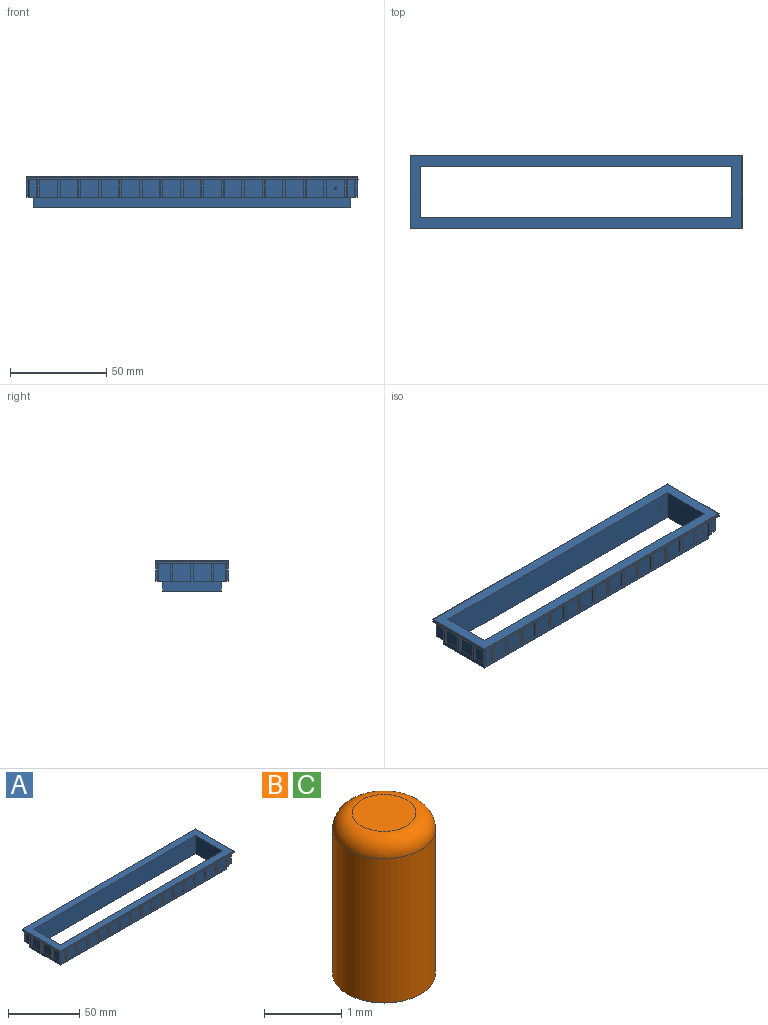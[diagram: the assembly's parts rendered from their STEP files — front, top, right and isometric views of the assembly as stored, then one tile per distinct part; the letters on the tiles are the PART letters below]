
ASSEMBLY  parts=3 mates=2
PART A: 299 faces, bbox 172.7x38.1x15.7 mm
  f0: plane 9.38x1.14mm, normal (0,0,-1), area 10.4mm2, adj f62,f134,f136,f254,f255,f288
  f1: plane 9.38x1.14mm, normal (0,0,-1), area 10.4mm2, adj f63,f131,f133,f256,f257,f288
  f2: plane 9.38x1.14mm, normal (0,0,-1), area 10.4mm2, adj f64,f128,f130,f258,f259,f288
  f3: plane 9.38x1.14mm, normal (0,0,-1), area 10.4mm2, adj f65,f125,f127,f260,f261,f288
  f4: plane 9.38x1.14mm, normal (0,0,-1), area 10.4mm2, adj f66,f122,f124,f262,f263,f288
  f5: plane 9.38x1.14mm, normal (0,0,-1), area 10.4mm2, adj f67,f119,f121,f264,f265,f288
  f6: plane 9.38x1.14mm, normal (0,0,-1), area 10.4mm2, adj f68,f116,f118,f266,f267,f288
  f7: plane 9.38x1.14mm, normal (0,0,-1), area 10.4mm2, adj f69,f113,f115,f268,f269,f288
  f8: plane 9.38x1.14mm, normal (0,0,-1), area 10.4mm2, adj f70,f110,f112,f270,f271,f288
  f9: plane 9.38x1.14mm, normal (0,0,-1), area 10.4mm2, adj f71,f107,f109,f272,f273,f288
  f10: plane 9.38x1.14mm, normal (0,0,-1), area 10.4mm2, adj f72,f104,f106,f274,f275,f288
  f11: plane 9.38x1.14mm, normal (0,0,-1), area 10.4mm2, adj f73,f101,f103,f276,f277,f288
  f12: plane 9.38x1.14mm, normal (0,0,-1), area 10.4mm2, adj f74,f98,f100,f278,f279,f288
  f13: plane 9.38x1.14mm, normal (0,0,-1), area 10.4mm2, adj f75,f95,f97,f280,f281,f288
  f14: plane 9.38x1.14mm, normal (0,0,-1), area 10.4mm2, adj f76,f91,f94,f282,f283,f288
  f15: plane 7.64x5.72mm, normal (0,0,-1), area 13.7mm2, adj f77,f81,f93,f195,f216,f284,f286,f288
  f16: plane 9.38x1.14mm, normal (0,0,-1), area 10.4mm2, adj f43,f192,f194,f215,f218,f286
  f17: plane 9.38x1.14mm, normal (0,0,-1), area 10.4mm2, adj f44,f189,f191,f217,f220,f286
  f18: plane 7.64x5.72mm, normal (0,0,-1), area 13.7mm2, adj f45,f51,f169,f188,f219,f231,f285,f286
  f19: plane 9.38x1.14mm, normal (0,0,-1), area 10.4mm2, adj f59,f145,f170,f232,f247,f285
  f20: plane 9.38x1.14mm, normal (0,0,-1), area 10.4mm2, adj f52,f147,f166,f233,f248,f285
  f21: plane 9.38x1.14mm, normal (0,0,-1), area 10.4mm2, adj f49,f168,f175,f227,f234,f285
  f22: plane 9.38x1.14mm, normal (0,0,-1), area 10.4mm2, adj f61,f139,f176,f228,f251,f285
  f23: plane 9.38x1.14mm, normal (0,0,-1), area 10.4mm2, adj f57,f140,f151,f243,f252,f285
  f24: plane 9.38x1.14mm, normal (0,0,-1), area 10.4mm2, adj f46,f153,f184,f221,f244,f285
  f25: plane 9.38x1.14mm, normal (0,0,-1), area 10.4mm2, adj f60,f142,f186,f222,f249,f285
  f26: plane 9.38x1.14mm, normal (0,0,-1), area 10.4mm2, adj f54,f144,f160,f237,f250,f285
  f27: plane 9.38x1.14mm, normal (0,0,-1), area 10.4mm2, adj f47,f162,f181,f223,f238,f285
  f28: plane 9.38x1.14mm, normal (0,0,-1), area 10.4mm2, adj f58,f148,f182,f224,f245,f285
  f29: plane 9.38x1.14mm, normal (0,0,-1), area 10.4mm2, adj f48,f150,f178,f225,f246,f285
  f30: plane 9.38x1.14mm, normal (0,0,-1), area 10.4mm2, adj f50,f172,f179,f226,f229,f285
  f31: plane 9.38x1.14mm, normal (0,0,-1), area 10.4mm2, adj f55,f157,f173,f230,f239,f285
  f32: plane 9.38x1.14mm, normal (0,0,-1), area 10.4mm2, adj f56,f154,f159,f240,f241,f285
  f33: plane 9.38x1.14mm, normal (0,0,-1), area 10.4mm2, adj f53,f155,f163,f235,f242,f285
  f34: plane 7.64x5.69mm, normal (0,0,-1), area 13.7mm2, adj f41,f80,f164,f201,f212,f236,f285,f287
  f35: plane 9.38x1.14mm, normal (0,0,-1), area 10.4mm2, adj f39,f200,f204,f210,f211,f287
  f36: plane 9.38x1.14mm, normal (0,0,-1), area 10.4mm2, adj f42,f198,f203,f209,f214,f287
  f37: plane 165.1x30.48mm, normal (0,0,-1), area 682.8mm2, adj f83,f84,f85,f86,f205,f206,f207,f208
  f38: plane 172.47x37.85mm, normal (0,0,1), area 2177.7mm2, adj f205,f206,f207,f208,f289,f290,f291,f292
  f39: plane 9.13x9.12mm, normal (1,0,0), area 83.2mm2, adj f35,f82,f200,f204
  f40: plane 7.64x5.69mm, normal (0,0,-1), area 13.7mm2, adj f78,f79,f137,f197,f213,f253,f287,f288
  f41: plane 9.12x5.86mm, normal (1,0,0), area 53.4mm2, adj f34,f82,f201,f294
  f42: plane 9.13x9.12mm, normal (1,0,0), area 83.2mm2, adj f36,f82,f198,f203
  f43: plane 9.13x9.12mm, normal (-1,0,0), area 83.2mm2, adj f16,f82,f192,f194
  f44: plane 9.13x9.12mm, normal (-1,0,0), area 83.2mm2, adj f17,f82,f189,f191
  f45: plane 9.12x5.86mm, normal (-1,0,0), area 53.4mm2, adj f18,f82,f188,f295
  f46: plane 9.13x9.12mm, normal (0,1,0), area 83.2mm2, adj f24,f82,f153,f184
  f47: plane 9.13x9.12mm, normal (0,1,0), area 83.2mm2, adj f27,f82,f162,f181
  f48: plane 9.13x9.12mm, normal (0,1,0), area 83.2mm2, adj f29,f82,f150,f178
  f49: plane 9.13x9.12mm, normal (0,1,0), area 83.2mm2, adj f21,f82,f168,f175
  f50: plane 9.13x9.12mm, normal (0,1,0), area 83.2mm2, adj f30,f82,f172,f179
  f51: plane 9.12x3.94mm, normal (0,1,0), area 35.9mm2, adj f18,f82,f169,f295
  f52: plane 9.13x9.12mm, normal (0,1,0), area 83.2mm2, adj f20,f82,f147,f166
  f53: plane 9.13x9.12mm, normal (0,1,0), area 81.7mm2, adj f33,f82,f155,f163,f297
  f54: plane 9.13x9.12mm, normal (0,1,0), area 83.2mm2, adj f26,f82,f144,f160
  f55: plane 9.13x9.12mm, normal (0,1,0), area 83.2mm2, adj f31,f82,f157,f173
  f56: plane 9.13x9.12mm, normal (0,1,0), area 83.2mm2, adj f32,f82,f154,f159
  f57: plane 9.13x9.12mm, normal (0,1,0), area 83.2mm2, adj f23,f82,f140,f151
  f58: plane 9.13x9.12mm, normal (0,1,0), area 83.2mm2, adj f28,f82,f148,f182
  f59: plane 9.13x9.12mm, normal (0,1,0), area 83.2mm2, adj f19,f82,f145,f170
  f60: plane 9.13x9.12mm, normal (0,1,0), area 83.2mm2, adj f25,f82,f142,f186
  f61: plane 9.13x9.12mm, normal (0,1,0), area 83.2mm2, adj f22,f82,f139,f176
  f62: plane 9.13x9.12mm, normal (0,-1,0), area 81.7mm2, adj f0,f82,f134,f136,f298
  f63: plane 9.13x9.12mm, normal (0,-1,0), area 83.2mm2, adj f1,f82,f131,f133
  f64: plane 9.13x9.12mm, normal (0,-1,0), area 83.2mm2, adj f2,f82,f128,f130
  f65: plane 9.13x9.12mm, normal (0,-1,0), area 83.2mm2, adj f3,f82,f125,f127
  f66: plane 9.13x9.12mm, normal (0,-1,0), area 83.2mm2, adj f4,f82,f122,f124
  f67: plane 9.13x9.12mm, normal (0,-1,0), area 83.2mm2, adj f5,f82,f119,f121
  f68: plane 9.13x9.12mm, normal (0,-1,0), area 83.2mm2, adj f6,f82,f116,f118
  f69: plane 9.13x9.12mm, normal (0,-1,0), area 83.2mm2, adj f7,f82,f113,f115
  f70: plane 9.13x9.12mm, normal (0,-1,0), area 83.2mm2, adj f8,f82,f110,f112
  f71: plane 9.13x9.12mm, normal (0,-1,0), area 83.2mm2, adj f9,f82,f107,f109
  f72: plane 9.13x9.12mm, normal (0,-1,0), area 83.2mm2, adj f10,f82,f104,f106
  f73: plane 9.13x9.12mm, normal (0,-1,0), area 83.2mm2, adj f11,f82,f101,f103
  f74: plane 9.13x9.12mm, normal (0,-1,0), area 83.2mm2, adj f12,f82,f98,f100
  f75: plane 9.13x9.12mm, normal (0,-1,0), area 83.2mm2, adj f13,f82,f95,f97
  f76: plane 9.13x9.12mm, normal (0,-1,0), area 83.2mm2, adj f14,f82,f91,f94
  f77: plane 9.12x3.94mm, normal (0,-1,0), area 35.9mm2, adj f15,f82,f93,f296
  f78: plane 9.12x3.91mm, normal (0,-1,0), area 35.7mm2, adj f40,f82,f137,f293
  f79: plane 9.12x5.86mm, normal (1,0,0), area 53.4mm2, adj f40,f82,f197,f293
  f80: plane 9.12x3.91mm, normal (0,1,0), area 35.7mm2, adj f34,f82,f164,f294
  f81: plane 9.12x5.86mm, normal (-1,0,0), area 53.4mm2, adj f15,f82,f195,f296
  f82: plane 172.47x37.85mm, normal (0,0,-1), area 1085.1mm2, adj f39,f41,f42,f43,f44,f45,f46,f47
  f83: plane 165.1x5.08mm, normal (0,-1,0), area 838.7mm2, adj f37,f82,f84,f86
  f84: plane 30.48x5.08mm, normal (-1,0,0), area 154.8mm2, adj f37,f82,f83,f85
  f85: plane 165.1x5.08mm, normal (0,1,0), area 838.7mm2, adj f37,f82,f84,f86
  f86: plane 30.48x5.08mm, normal (1,0,0), area 154.8mm2, adj f37,f82,f83,f85
  f87: plane 172.72x1.27mm, normal (0,1,0), area 219.4mm2, adj f88,f90,f285,f289
  f88: plane 38.1x1.27mm, normal (-1,0,0), area 48.4mm2, adj f87,f89,f286,f290
  f89: plane 172.72x1.27mm, normal (0,-1,0), area 219.4mm2, adj f88,f90,f288,f292
  f90: plane 38.1x1.27mm, normal (1,0,0), area 48.4mm2, adj f87,f89,f287,f291
  f91: plane 9.12x1.02mm, normal (1,0,0), area 9.3mm2, adj f14,f76,f82,f283
  f92: plane 9.12x1.27mm, normal (0,-1,0), area 11.6mm2, adj f82,f283,f284,f288
  f93: plane 9.12x1.02mm, normal (-1,0,0), area 9.3mm2, adj f15,f77,f82,f284
  f94: plane 9.12x1.02mm, normal (-1,0,0), area 9.3mm2, adj f14,f76,f82,f282
  f95: plane 9.12x1.02mm, normal (1,0,0), area 9.3mm2, adj f13,f75,f82,f281
  f96: plane 9.12x1.27mm, normal (0,-1,0), area 11.6mm2, adj f82,f281,f282,f288
  f97: plane 9.12x1.02mm, normal (-1,0,0), area 9.3mm2, adj f13,f75,f82,f280
  f98: plane 9.12x1.02mm, normal (1,0,0), area 9.3mm2, adj f12,f74,f82,f279
  f99: plane 9.12x1.27mm, normal (0,-1,0), area 11.6mm2, adj f82,f279,f280,f288
  f100: plane 9.12x1.02mm, normal (-1,0,0), area 9.3mm2, adj f12,f74,f82,f278
  f101: plane 9.12x1.02mm, normal (1,0,0), area 9.3mm2, adj f11,f73,f82,f277
  f102: plane 9.12x1.27mm, normal (0,-1,0), area 11.6mm2, adj f82,f277,f278,f288
  f103: plane 9.12x1.02mm, normal (-1,0,0), area 9.3mm2, adj f11,f73,f82,f276
  f104: plane 9.12x1.02mm, normal (1,0,0), area 9.3mm2, adj f10,f72,f82,f275
  f105: plane 9.12x1.27mm, normal (0,-1,0), area 11.6mm2, adj f82,f275,f276,f288
  f106: plane 9.12x1.02mm, normal (-1,0,0), area 9.3mm2, adj f10,f72,f82,f274
  f107: plane 9.12x1.02mm, normal (1,0,0), area 9.3mm2, adj f9,f71,f82,f273
  f108: plane 9.12x1.27mm, normal (0,-1,0), area 11.6mm2, adj f82,f273,f274,f288
  f109: plane 9.12x1.02mm, normal (-1,0,0), area 9.3mm2, adj f9,f71,f82,f272
  f110: plane 9.12x1.02mm, normal (1,0,0), area 9.3mm2, adj f8,f70,f82,f271
  f111: plane 9.12x1.27mm, normal (0,-1,0), area 11.6mm2, adj f82,f271,f272,f288
  f112: plane 9.12x1.02mm, normal (-1,0,0), area 9.3mm2, adj f8,f70,f82,f270
  f113: plane 9.12x1.02mm, normal (1,0,0), area 9.3mm2, adj f7,f69,f82,f269
  f114: plane 9.12x1.27mm, normal (0,-1,0), area 11.6mm2, adj f82,f269,f270,f288
  f115: plane 9.12x1.02mm, normal (-1,0,0), area 9.3mm2, adj f7,f69,f82,f268
  f116: plane 9.12x1.02mm, normal (1,0,0), area 9.3mm2, adj f6,f68,f82,f267
  f117: plane 9.12x1.27mm, normal (0,-1,0), area 11.6mm2, adj f82,f267,f268,f288
  f118: plane 9.12x1.02mm, normal (-1,0,0), area 9.3mm2, adj f6,f68,f82,f266
  f119: plane 9.12x1.02mm, normal (1,0,0), area 9.3mm2, adj f5,f67,f82,f265
  f120: plane 9.12x1.27mm, normal (0,-1,0), area 11.6mm2, adj f82,f265,f266,f288
  f121: plane 9.12x1.02mm, normal (-1,0,0), area 9.3mm2, adj f5,f67,f82,f264
  f122: plane 9.12x1.02mm, normal (1,0,0), area 9.3mm2, adj f4,f66,f82,f263
  f123: plane 9.12x1.27mm, normal (0,-1,0), area 11.6mm2, adj f82,f263,f264,f288
  f124: plane 9.12x1.02mm, normal (-1,0,0), area 9.3mm2, adj f4,f66,f82,f262
  f125: plane 9.12x1.02mm, normal (1,0,0), area 9.3mm2, adj f3,f65,f82,f261
  f126: plane 9.12x1.27mm, normal (0,-1,0), area 11.6mm2, adj f82,f261,f262,f288
  f127: plane 9.12x1.02mm, normal (-1,0,0), area 9.3mm2, adj f3,f65,f82,f260
  f128: plane 9.12x1.02mm, normal (1,0,0), area 9.3mm2, adj f2,f64,f82,f259
  f129: plane 9.12x1.27mm, normal (0,-1,0), area 11.6mm2, adj f82,f259,f260,f288
  f130: plane 9.12x1.02mm, normal (-1,0,0), area 9.3mm2, adj f2,f64,f82,f258
  f131: plane 9.12x1.02mm, normal (1,0,0), area 9.3mm2, adj f1,f63,f82,f257
  f132: plane 9.12x1.27mm, normal (0,-1,0), area 11.6mm2, adj f82,f257,f258,f288
  f133: plane 9.12x1.02mm, normal (-1,0,0), area 9.3mm2, adj f1,f63,f82,f256
  f134: plane 9.12x1.02mm, normal (1,0,0), area 9.3mm2, adj f0,f62,f82,f255
  f135: plane 9.12x1.27mm, normal (0,-1,0), area 11.6mm2, adj f82,f255,f256,f288
  f136: plane 9.12x1.02mm, normal (-1,0,0), area 9.3mm2, adj f0,f62,f82,f254
  f137: plane 9.12x1.02mm, normal (1,0,0), area 9.3mm2, adj f40,f78,f82,f253
  f138: plane 9.12x1.27mm, normal (0,-1,0), area 11.6mm2, adj f82,f253,f254,f288
  f139: plane 9.12x1.02mm, normal (-1,0,0), area 9.3mm2, adj f22,f61,f82,f251
  f140: plane 9.12x1.02mm, normal (1,0,0), area 9.3mm2, adj f23,f57,f82,f252
  f141: plane 9.12x1.27mm, normal (0,1,0), area 11.6mm2, adj f82,f251,f252,f285
  f142: plane 9.12x1.02mm, normal (-1,0,0), area 9.3mm2, adj f25,f60,f82,f249
  f143: plane 9.12x1.27mm, normal (0,1,0), area 11.6mm2, adj f82,f249,f250,f285
  f144: plane 9.12x1.02mm, normal (1,0,0), area 9.3mm2, adj f26,f54,f82,f250
  f145: plane 9.12x1.02mm, normal (-1,0,0), area 9.3mm2, adj f19,f59,f82,f247
  f146: plane 9.12x1.27mm, normal (0,1,0), area 11.6mm2, adj f82,f247,f248,f285
  f147: plane 9.12x1.02mm, normal (1,0,0), area 9.3mm2, adj f20,f52,f82,f248
  f148: plane 9.12x1.02mm, normal (-1,0,0), area 9.3mm2, adj f28,f58,f82,f245
  f149: plane 9.12x1.27mm, normal (0,1,0), area 11.6mm2, adj f82,f245,f246,f285
  f150: plane 9.12x1.02mm, normal (1,0,0), area 9.3mm2, adj f29,f48,f82,f246
  f151: plane 9.12x1.02mm, normal (-1,0,0), area 9.3mm2, adj f23,f57,f82,f243
  f152: plane 9.12x1.27mm, normal (0,1,0), area 11.6mm2, adj f82,f243,f244,f285
  f153: plane 9.12x1.02mm, normal (1,0,0), area 9.3mm2, adj f24,f46,f82,f244
  f154: plane 9.12x1.02mm, normal (-1,0,0), area 9.3mm2, adj f32,f56,f82,f241
  f155: plane 9.12x1.02mm, normal (1,0,0), area 9.3mm2, adj f33,f53,f82,f242
  f156: plane 9.12x1.27mm, normal (0,1,0), area 11.6mm2, adj f82,f241,f242,f285
  f157: plane 9.12x1.02mm, normal (-1,0,0), area 9.3mm2, adj f31,f55,f82,f239
  f158: plane 9.12x1.27mm, normal (0,1,0), area 11.6mm2, adj f82,f239,f240,f285
  f159: plane 9.12x1.02mm, normal (1,0,0), area 9.3mm2, adj f32,f56,f82,f240
  f160: plane 9.12x1.02mm, normal (-1,0,0), area 9.3mm2, adj f26,f54,f82,f237
  f161: plane 9.12x1.27mm, normal (0,1,0), area 11.6mm2, adj f82,f237,f238,f285
  f162: plane 9.12x1.02mm, normal (1,0,0), area 9.3mm2, adj f27,f47,f82,f238
  f163: plane 9.12x1.02mm, normal (-1,0,0), area 9.3mm2, adj f33,f53,f82,f235
  f164: plane 9.12x1.02mm, normal (1,0,0), area 9.3mm2, adj f34,f80,f82,f236
  f165: plane 9.12x1.27mm, normal (0,1,0), area 11.6mm2, adj f82,f235,f236,f285
  f166: plane 9.12x1.02mm, normal (-1,0,0), area 9.3mm2, adj f20,f52,f82,f233
  f167: plane 9.12x1.27mm, normal (0,1,0), area 11.6mm2, adj f82,f233,f234,f285
  f168: plane 9.12x1.02mm, normal (1,0,0), area 9.3mm2, adj f21,f49,f82,f234
  f169: plane 9.12x1.02mm, normal (-1,0,0), area 9.3mm2, adj f18,f51,f82,f231
  f170: plane 9.12x1.02mm, normal (1,0,0), area 9.3mm2, adj f19,f59,f82,f232
  f171: plane 9.12x1.27mm, normal (0,1,0), area 11.6mm2, adj f82,f231,f232,f285
  f172: plane 9.12x1.02mm, normal (-1,0,0), area 9.3mm2, adj f30,f50,f82,f229
  f173: plane 9.12x1.02mm, normal (1,0,0), area 9.3mm2, adj f31,f55,f82,f230
  f174: plane 9.12x1.27mm, normal (0,1,0), area 11.6mm2, adj f82,f229,f230,f285
  f175: plane 9.12x1.02mm, normal (-1,0,0), area 9.3mm2, adj f21,f49,f82,f227
  f176: plane 9.12x1.02mm, normal (1,0,0), area 9.3mm2, adj f22,f61,f82,f228
  f177: plane 9.12x1.27mm, normal (0,1,0), area 11.6mm2, adj f82,f227,f228,f285
  f178: plane 9.12x1.02mm, normal (-1,0,0), area 9.3mm2, adj f29,f48,f82,f225
  f179: plane 9.12x1.02mm, normal (1,0,0), area 9.3mm2, adj f30,f50,f82,f226
  f180: plane 9.12x1.27mm, normal (0,1,0), area 11.6mm2, adj f82,f225,f226,f285
  f181: plane 9.12x1.02mm, normal (-1,0,0), area 9.3mm2, adj f27,f47,f82,f223
  f182: plane 9.12x1.02mm, normal (1,0,0), area 9.3mm2, adj f28,f58,f82,f224
  f183: plane 9.12x1.27mm, normal (0,1,0), area 11.6mm2, adj f82,f223,f224,f285
  f184: plane 9.12x1.02mm, normal (-1,0,0), area 9.3mm2, adj f24,f46,f82,f221
  f185: plane 9.12x1.27mm, normal (0,1,0), area 11.6mm2, adj f82,f221,f222,f285
  f186: plane 9.12x1.02mm, normal (1,0,0), area 9.3mm2, adj f25,f60,f82,f222
  f187: plane 9.12x1.27mm, normal (-1,0,0), area 11.6mm2, adj f82,f219,f220,f286
  f188: plane 9.12x1.02mm, normal (0,1,0), area 9.3mm2, adj f18,f45,f82,f219
  f189: plane 9.12x1.02mm, normal (0,-1,0), area 9.3mm2, adj f17,f44,f82,f220
  f190: plane 9.12x1.27mm, normal (-1,0,0), area 11.6mm2, adj f82,f217,f218,f286
  f191: plane 9.12x1.02mm, normal (0,1,0), area 9.3mm2, adj f17,f44,f82,f217
  f192: plane 9.12x1.02mm, normal (0,-1,0), area 9.3mm2, adj f16,f43,f82,f218
  f193: plane 9.12x1.27mm, normal (-1,0,0), area 11.6mm2, adj f82,f215,f216,f286
  f194: plane 9.12x1.02mm, normal (0,1,0), area 9.3mm2, adj f16,f43,f82,f215
  f195: plane 9.12x1.02mm, normal (0,-1,0), area 9.3mm2, adj f15,f81,f82,f216
  f196: plane 9.12x1.27mm, normal (1,0,0), area 11.6mm2, adj f82,f213,f214,f287
  f197: plane 9.12x1.02mm, normal (0,-1,0), area 9.3mm2, adj f40,f79,f82,f213
  f198: plane 9.12x1.02mm, normal (0,1,0), area 9.3mm2, adj f36,f42,f82,f214
  f199: plane 9.12x1.27mm, normal (1,0,0), area 11.6mm2, adj f82,f211,f212,f287
  f200: plane 9.12x1.02mm, normal (0,-1,0), area 9.3mm2, adj f35,f39,f82,f211
  f201: plane 9.12x1.02mm, normal (0,1,0), area 9.3mm2, adj f34,f41,f82,f212
  f202: plane 9.12x1.27mm, normal (1,0,0), area 11.6mm2, adj f82,f209,f210,f287
  f203: plane 9.12x1.02mm, normal (0,-1,0), area 9.3mm2, adj f36,f42,f82,f209
  f204: plane 9.12x1.02mm, normal (0,1,0), area 9.3mm2, adj f35,f39,f82,f210
  f205: plane 161.54x15.72mm, normal (0,1,0), area 2538.4mm2, adj f37,f38,f206,f208,f298
  f206: plane 26.92x15.72mm, normal (1,0,0), area 423.3mm2, adj f37,f38,f205,f207
  f207: plane 161.54x15.72mm, normal (0,-1,0), area 2538.4mm2, adj f37,f38,f206,f208,f297
  f208: plane 26.92x15.72mm, normal (-1,0,0), area 423.3mm2, adj f37,f38,f205,f207
  f209: cylinder r=0.13mm len=9.12mm, axis (0,0,-1), area 1.8mm2, adj f36,f82,f202,f203
  f210: cylinder r=0.13mm len=9.12mm, axis (0,0,1), area 1.8mm2, adj f35,f82,f202,f204
  f211: cylinder r=0.13mm len=9.12mm, axis (0,0,-1), area 1.8mm2, adj f35,f82,f199,f200
  f212: cylinder r=0.13mm len=9.12mm, axis (0,0,1), area 1.8mm2, adj f34,f82,f199,f201
  f213: cylinder r=0.13mm len=9.12mm, axis (0,0,-1), area 1.8mm2, adj f40,f82,f196,f197
  f214: cylinder r=0.13mm len=9.12mm, axis (0,0,1), area 1.8mm2, adj f36,f82,f196,f198
  f215: cylinder r=0.13mm len=9.12mm, axis (0,0,1), area 1.8mm2, adj f16,f82,f193,f194
  f216: cylinder r=0.13mm len=9.12mm, axis (0,0,-1), area 1.8mm2, adj f15,f82,f193,f195
  f217: cylinder r=0.13mm len=9.12mm, axis (0,0,1), area 1.8mm2, adj f17,f82,f190,f191
  f218: cylinder r=0.13mm len=9.12mm, axis (0,0,-1), area 1.8mm2, adj f16,f82,f190,f192
  f219: cylinder r=0.13mm len=9.12mm, axis (0,0,1), area 1.8mm2, adj f18,f82,f187,f188
  f220: cylinder r=0.13mm len=9.12mm, axis (0,0,-1), area 1.8mm2, adj f17,f82,f187,f189
  f221: cylinder r=0.13mm len=9.12mm, axis (0,0,1), area 1.8mm2, adj f24,f82,f184,f185
  f222: cylinder r=0.13mm len=9.12mm, axis (0,0,-1), area 1.8mm2, adj f25,f82,f185,f186
  f223: cylinder r=0.13mm len=9.12mm, axis (0,0,1), area 1.8mm2, adj f27,f82,f181,f183
  f224: cylinder r=0.13mm len=9.12mm, axis (0,0,-1), area 1.8mm2, adj f28,f82,f182,f183
  f225: cylinder r=0.13mm len=9.12mm, axis (0,0,1), area 1.8mm2, adj f29,f82,f178,f180
  f226: cylinder r=0.13mm len=9.12mm, axis (0,0,-1), area 1.8mm2, adj f30,f82,f179,f180
  f227: cylinder r=0.13mm len=9.12mm, axis (0,0,1), area 1.8mm2, adj f21,f82,f175,f177
  f228: cylinder r=0.13mm len=9.12mm, axis (0,0,-1), area 1.8mm2, adj f22,f82,f176,f177
  f229: cylinder r=0.13mm len=9.12mm, axis (0,0,1), area 1.8mm2, adj f30,f82,f172,f174
  f230: cylinder r=0.13mm len=9.12mm, axis (0,0,-1), area 1.8mm2, adj f31,f82,f173,f174
  f231: cylinder r=0.13mm len=9.12mm, axis (0,0,1), area 1.8mm2, adj f18,f82,f169,f171
  f232: cylinder r=0.13mm len=9.12mm, axis (0,0,-1), area 1.8mm2, adj f19,f82,f170,f171
  f233: cylinder r=0.13mm len=9.12mm, axis (0,0,1), area 1.8mm2, adj f20,f82,f166,f167
  f234: cylinder r=0.13mm len=9.12mm, axis (0,0,-1), area 1.8mm2, adj f21,f82,f167,f168
  f235: cylinder r=0.13mm len=9.12mm, axis (0,0,1), area 1.8mm2, adj f33,f82,f163,f165
  f236: cylinder r=0.13mm len=9.12mm, axis (0,0,-1), area 1.8mm2, adj f34,f82,f164,f165
  f237: cylinder r=0.13mm len=9.12mm, axis (0,0,1), area 1.8mm2, adj f26,f82,f160,f161
  f238: cylinder r=0.13mm len=9.12mm, axis (0,0,-1), area 1.8mm2, adj f27,f82,f161,f162
  f239: cylinder r=0.13mm len=9.12mm, axis (0,0,1), area 1.8mm2, adj f31,f82,f157,f158
  f240: cylinder r=0.13mm len=9.12mm, axis (0,0,-1), area 1.8mm2, adj f32,f82,f158,f159
  f241: cylinder r=0.13mm len=9.12mm, axis (0,0,1), area 1.8mm2, adj f32,f82,f154,f156
  f242: cylinder r=0.13mm len=9.12mm, axis (0,0,-1), area 1.8mm2, adj f33,f82,f155,f156
  f243: cylinder r=0.13mm len=9.12mm, axis (0,0,1), area 1.8mm2, adj f23,f82,f151,f152
  f244: cylinder r=0.13mm len=9.12mm, axis (0,0,-1), area 1.8mm2, adj f24,f82,f152,f153
  f245: cylinder r=0.13mm len=9.12mm, axis (0,0,1), area 1.8mm2, adj f28,f82,f148,f149
  f246: cylinder r=0.13mm len=9.12mm, axis (0,0,-1), area 1.8mm2, adj f29,f82,f149,f150
  f247: cylinder r=0.13mm len=9.12mm, axis (0,0,1), area 1.8mm2, adj f19,f82,f145,f146
  f248: cylinder r=0.13mm len=9.12mm, axis (0,0,-1), area 1.8mm2, adj f20,f82,f146,f147
  f249: cylinder r=0.13mm len=9.12mm, axis (0,0,1), area 1.8mm2, adj f25,f82,f142,f143
  f250: cylinder r=0.13mm len=9.12mm, axis (0,0,-1), area 1.8mm2, adj f26,f82,f143,f144
  f251: cylinder r=0.13mm len=9.12mm, axis (0,0,1), area 1.8mm2, adj f22,f82,f139,f141
  f252: cylinder r=0.13mm len=9.12mm, axis (0,0,-1), area 1.8mm2, adj f23,f82,f140,f141
  f253: cylinder r=0.13mm len=9.12mm, axis (0,0,-1), area 1.8mm2, adj f40,f82,f137,f138
  f254: cylinder r=0.13mm len=9.12mm, axis (0,0,1), area 1.8mm2, adj f0,f82,f136,f138
  f255: cylinder r=0.13mm len=9.12mm, axis (0,0,-1), area 1.8mm2, adj f0,f82,f134,f135
  f256: cylinder r=0.13mm len=9.12mm, axis (0,0,1), area 1.8mm2, adj f1,f82,f133,f135
  f257: cylinder r=0.13mm len=9.12mm, axis (0,0,-1), area 1.8mm2, adj f1,f82,f131,f132
  f258: cylinder r=0.13mm len=9.12mm, axis (0,0,1), area 1.8mm2, adj f2,f82,f130,f132
  f259: cylinder r=0.13mm len=9.12mm, axis (0,0,-1), area 1.8mm2, adj f2,f82,f128,f129
  f260: cylinder r=0.13mm len=9.12mm, axis (0,0,1), area 1.8mm2, adj f3,f82,f127,f129
  f261: cylinder r=0.13mm len=9.12mm, axis (0,0,-1), area 1.8mm2, adj f3,f82,f125,f126
  f262: cylinder r=0.13mm len=9.12mm, axis (0,0,1), area 1.8mm2, adj f4,f82,f124,f126
  f263: cylinder r=0.13mm len=9.12mm, axis (0,0,-1), area 1.8mm2, adj f4,f82,f122,f123
  f264: cylinder r=0.13mm len=9.12mm, axis (0,0,1), area 1.8mm2, adj f5,f82,f121,f123
  f265: cylinder r=0.13mm len=9.12mm, axis (0,0,-1), area 1.8mm2, adj f5,f82,f119,f120
  f266: cylinder r=0.13mm len=9.12mm, axis (0,0,1), area 1.8mm2, adj f6,f82,f118,f120
  f267: cylinder r=0.13mm len=9.12mm, axis (0,0,-1), area 1.8mm2, adj f6,f82,f116,f117
  f268: cylinder r=0.13mm len=9.12mm, axis (0,0,1), area 1.8mm2, adj f7,f82,f115,f117
  f269: cylinder r=0.13mm len=9.12mm, axis (0,0,-1), area 1.8mm2, adj f7,f82,f113,f114
  f270: cylinder r=0.13mm len=9.12mm, axis (0,0,1), area 1.8mm2, adj f8,f82,f112,f114
  f271: cylinder r=0.13mm len=9.12mm, axis (0,0,-1), area 1.8mm2, adj f8,f82,f110,f111
  f272: cylinder r=0.13mm len=9.12mm, axis (0,0,1), area 1.8mm2, adj f9,f82,f109,f111
  f273: cylinder r=0.13mm len=9.12mm, axis (0,0,-1), area 1.8mm2, adj f9,f82,f107,f108
  f274: cylinder r=0.13mm len=9.12mm, axis (0,0,1), area 1.8mm2, adj f10,f82,f106,f108
  f275: cylinder r=0.13mm len=9.12mm, axis (0,0,-1), area 1.8mm2, adj f10,f82,f104,f105
  f276: cylinder r=0.13mm len=9.12mm, axis (0,0,1), area 1.8mm2, adj f11,f82,f103,f105
  f277: cylinder r=0.13mm len=9.12mm, axis (0,0,-1), area 1.8mm2, adj f11,f82,f101,f102
  f278: cylinder r=0.13mm len=9.12mm, axis (0,0,1), area 1.8mm2, adj f12,f82,f100,f102
  f279: cylinder r=0.13mm len=9.12mm, axis (0,0,-1), area 1.8mm2, adj f12,f82,f98,f99
  f280: cylinder r=0.13mm len=9.12mm, axis (0,0,1), area 1.8mm2, adj f13,f82,f97,f99
  f281: cylinder r=0.13mm len=9.12mm, axis (0,0,-1), area 1.8mm2, adj f13,f82,f95,f96
  f282: cylinder r=0.13mm len=9.12mm, axis (0,0,1), area 1.8mm2, adj f14,f82,f94,f96
  f283: cylinder r=0.13mm len=9.12mm, axis (0,0,-1), area 1.8mm2, adj f14,f82,f91,f92
  f284: cylinder r=0.13mm len=9.12mm, axis (0,0,1), area 1.8mm2, adj f15,f82,f92,f93
  f285: cylinder r=0.13mm len=172.72mm, axis (-1,0,0), area 34.4mm2, adj f18,f19,f20,f21,f22,f23,f24,f25
  f286: cylinder r=0.13mm len=38.1mm, axis (0,-1,0), area 7.6mm2, adj f15,f16,f17,f18,f88,f187,f190,f193
  f287: cylinder r=0.13mm len=38.1mm, axis (0,1,0), area 7.6mm2, adj f34,f35,f36,f40,f90,f196,f199,f202
  f288: cylinder r=0.13mm len=172.72mm, axis (1,0,0), area 34.4mm2, adj f0,f1,f2,f3,f4,f5,f6,f7
  f289: cylinder r=0.13mm len=172.72mm, axis (1,0,0), area 34.4mm2, adj f38,f87,f290,f291
  f290: cylinder r=0.13mm len=38.1mm, axis (0,1,0), area 7.6mm2, adj f38,f88,f289,f292
  f291: cylinder r=0.13mm len=38.1mm, axis (0,-1,0), area 7.6mm2, adj f38,f90,f289,f292
  f292: cylinder r=0.13mm len=172.72mm, axis (-1,0,0), area 34.4mm2, adj f38,f89,f290,f291
  f293: cylinder r=0.51mm len=9.12mm, axis (0,0,1), area 7.3mm2, adj f40,f78,f79,f82
  f294: cylinder r=0.51mm len=9.12mm, axis (0,0,-1), area 7.3mm2, adj f34,f41,f80,f82
  f295: cylinder r=0.51mm len=9.12mm, axis (0,0,1), area 7.3mm2, adj f18,f45,f51,f82
  f296: cylinder r=0.51mm len=9.12mm, axis (0,0,-1), area 7.3mm2, adj f15,f77,f81,f82
  f297: cylinder r=0.7mm len=4.32mm, axis (0,1,0), area 19mm2, adj f53,f207
  f298: cylinder r=0.7mm len=4.32mm, axis (0,1,0), area 19mm2, adj f62,f205
PART B: 4 faces, bbox 1.4x1.4x2.5 mm
  f0: cylinder r=0.67mm len=2.29mm, axis (0,0,-1), area 9.6mm2, adj f2,f3
  f1: plane 0.83x0.83mm, normal (0,0,1), area 0.5mm2, adj f3
  f2: plane 1.33x1.33mm, normal (0,0,-1), area 1.4mm2, adj f0
  f3: torus R=0.41mm, axis (0,0,1), area 1.4mm2, adj f0,f1
PART C: same geometry as B
PLACE A rot(axis=(0.25,-0.97,0),0deg) t=(8.55,-15.67,5.38)mm
PLACE B rot(axis=(-0.58,0.58,0.58),120deg) t=(83.14,0.65,9.94)mm
PLACE C rot(axis=(0.58,-0.58,0.58),120deg) t=(83.14,-32.02,9.94)mm
MATE cylindrical B.f0 <-> A.f297  axis (0,-1,0) through (83.14,1.8,9.94)mm
MATE cylindrical C.f0 <-> A.f297  axis (0,1,0) through (83.14,-33.16,9.94)mm
